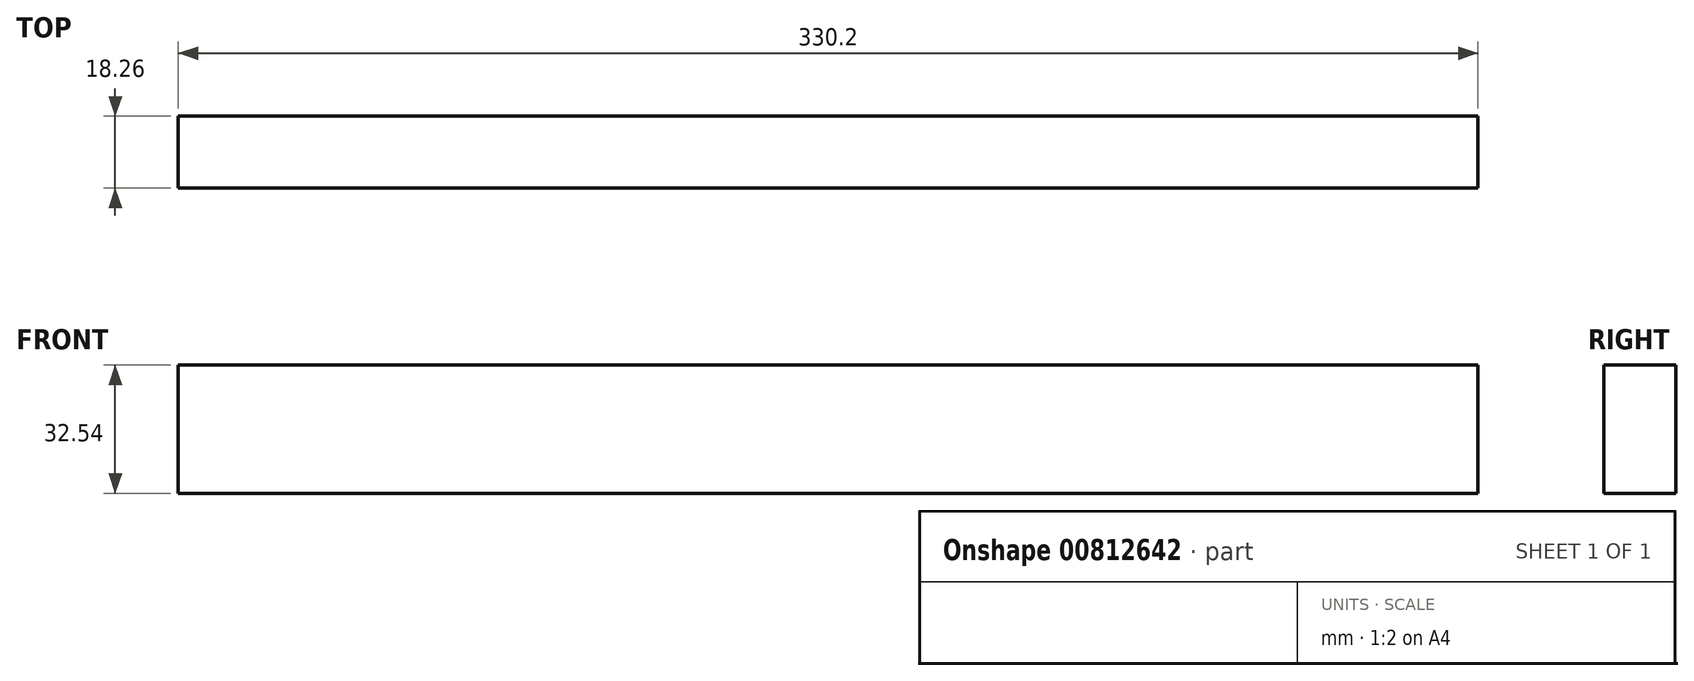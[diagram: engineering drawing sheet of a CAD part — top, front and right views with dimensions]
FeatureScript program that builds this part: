
annotation { "Feature Type Name" : "Feature", "Feature Type Description" : "" }
export const myFeature = defineFeature(function(context is Context, id is Id, definition is map)
    precondition{}
    {
        {
            var Q0;
            Q0=qCreatedBy(makeId("Front.planeOp"),FACE);
            var sketch = newSketch(context, id + "F0", { "sketchPlane" : qUnion([Q0])});
            skLineSegment(sketch, "E0.bottom", {"start": v(165.1, 16.27) * mm, "end": v(-165.1, 16.27) * mm});
            skLineSegment(sketch, "E0.top", {"start": v(165.1, -16.27) * mm, "end": v(-165.1, -16.27) * mm});
            skLineSegment(sketch, "E0.left", {"start": v(165.1, 16.27) * mm, "end": v(165.1, -16.27) * mm});
            skLineSegment(sketch, "E0.right", {"start": v(-165.1, 16.27) * mm, "end": v(-165.1, -16.27) * mm});
            skPoint(sketch, "E0.middle", {"position": v(0, 0) * mm});
            skSolve(sketch);
        }
        {
            var Q0;
            Q0=qSketchRegion(id+"F0",true);
            extrude(context, id + "F1", {"entities" : qUnion([Q0]), "depth" : 18.26 * mm, "offsetDistance" : 25.4 * mm});
        }
    });
